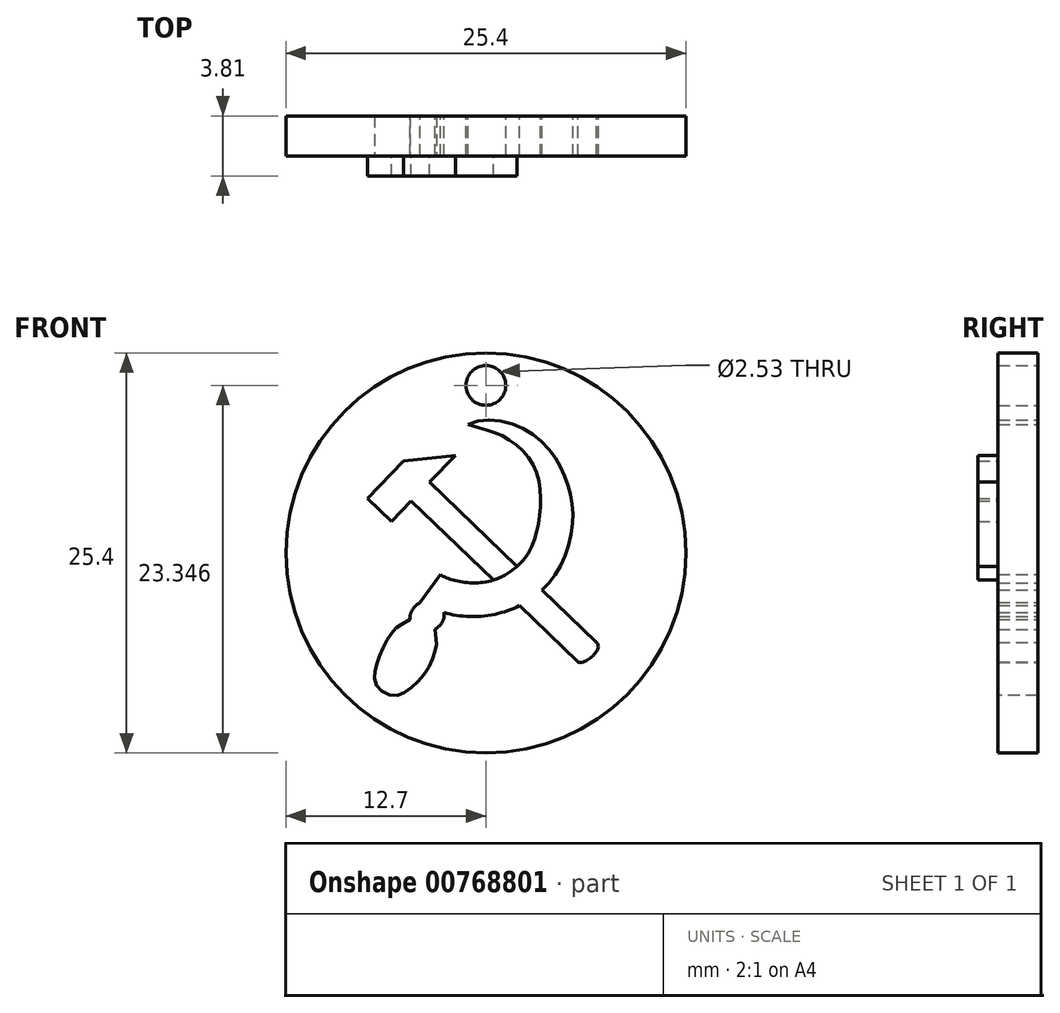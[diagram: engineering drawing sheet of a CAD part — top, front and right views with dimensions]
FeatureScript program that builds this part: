
annotation { "Feature Type Name" : "Feature", "Feature Type Description" : "" }
export const myFeature = defineFeature(function(context is Context, id is Id, definition is map)
    precondition{}
    {
        {
            var Q0;
            Q0=qCreatedBy(makeId("Front.planeOp"),FACE);
            var sketch = newSketch(context, id + "F0", { "sketchPlane" : qUnion([Q0])});
            skCircle(sketch, "E0", {"center": v(0, 0) * mm, "radius": 12.7 * mm});
            skCircle(sketch, "E1", {"center": v(0, 10.65) * mm, "radius": 1.27 * mm});
            skLineSegment(sketch, "E2", {"start": v(-7.53, 3.47) * mm, "end": v(-6, 2) * mm});
            skLineSegment(sketch, "E3", {"start": v(-7.53, 3.47) * mm, "end": v(-5.23, 5.85) * mm});
            skLineSegment(sketch, "E4", {"start": v(-6, 2) * mm, "end": v(-4.74, 3.3) * mm});
            skLineSegment(sketch, "E5", {"start": v(-1.94, 6.2) * mm, "end": v(-5.23, 5.85) * mm});
            skLineSegment(sketch, "E6", {"start": v(-4.74, 3.3) * mm, "end": v(0.47, -1.72) * mm});
            skLineSegment(sketch, "E7", {"start": v(-3.57, 4.51) * mm, "end": v(1.99, -0.84) * mm});
            skFitSpline(sketch, "E8", {"points": [v(7.03, -5.7) * mm, v(5.86, -6.91) * mm], "startDerivative": vector(1.48, -1.28) * mm, "endDerivative": vector(-1, 0.86) * mm});
            skLineSegment(sketch, "E9.trimOffspring", {"start": v(-3.57, 4.51) * mm, "end": v(-1.94, 6.2) * mm});
            skFitSpline(sketch, "E10", {"points": [v(-2.89, -1.37) * mm, v(-0.15, -1.86) * mm, v(2.5, -0.28) * mm, v(3.4, 2.29) * mm, v(3.1, 5.4) * mm, v(0.88, 7.52) * mm, v(-1.13, 8.15) * mm], "startDerivative": vector(9.05, -6.27) * mm, "endDerivative": vector(-9.41, 3.14) * mm});
            skFitSpline(sketch, "E11", {"points": [v(-1.13, 8.15) * mm, v(1.82, 8.15) * mm, v(4.18, 6.36) * mm, v(5.24, 4.2) * mm, v(5.52, 1.99) * mm, v(4.73, -0.8) * mm, v(3.17, -2.69) * mm, v(0.58, -3.9) * mm, v(-2.65, -3.77) * mm], "startDerivative": vector(18.3, 9.86) * mm, "endDerivative": vector(-19.6, 6.72) * mm});
            skLineSegment(sketch, "E12", {"start": v(-2.89, -1.37) * mm, "end": v(-4.2, -3.15) * mm});
            skFitSpline(sketch, "E13", {"points": [v(-2.65, -3.77) * mm, v(-3.23, -4.86) * mm], "startDerivative": vector(0.09, -1.86) * mm, "endDerivative": vector(-0.92, -0.75) * mm});
            skFitSpline(sketch, "E14", {"points": [v(-4.2, -3.15) * mm, v(-4.8, -4.23) * mm], "startDerivative": vector(-1.56, -0.98) * mm, "endDerivative": vector(0.16, -1.07) * mm});
            skFitSpline(sketch, "E15", {"points": [v(-4.8, -4.23) * mm, v(-5.85, -4.92) * mm, v(-6.57, -6.11) * mm, v(-7, -7.4) * mm, v(-6.93, -8.45) * mm, v(-5.8, -9.05) * mm, v(-4.66, -8.48) * mm, v(-3.6, -7.2) * mm, v(-3.16, -5.94) * mm, v(-3.23, -4.86) * mm], "startDerivative": vector(-16.95, -8.14) * mm, "endDerivative": vector(-2.6, 18.44) * mm});
            skLineSegment(sketch, "E16.trimOffspring", {"start": v(2.15, -3.34) * mm, "end": v(5.86, -6.91) * mm});
            skLineSegment(sketch, "E17.trimOffspring", {"start": v(3.56, -2.36) * mm, "end": v(7.03, -5.7) * mm});
            skFitSpline(sketch, "E18.trimOffspring", {"points": [v(-1.13, 8.15) * mm, v(1.82, 8.15) * mm, v(4.18, 6.36) * mm, v(5.24, 4.2) * mm, v(5.52, 1.99) * mm, v(4.73, -0.8) * mm, v(3.17, -2.69) * mm, v(0.58, -3.9) * mm, v(-2.65, -3.77) * mm], "startDerivative": vector(18.3, 9.86) * mm, "endDerivative": vector(-19.6, 6.72) * mm});
            skSolve(sketch);
        }
        {
            var Q0;
            Q0=makeQuery(id+"F0.imprint","IMPRINT",FACE,{"disambiguationData":[TD([[makeQuery(id+"F0.imprint","IMPRINT",EDGE,{"derivedFrom":sQuery(id+"F0.wireOp",EDGE,"E0")}),1.0]])]});
            extrude(context, id + "F1", {"entities" : qUnion([Q0]), "depth" : 2.54 * mm, "offsetDistance" : 25.4 * mm});
        }
        {
            var Q0;
            Q0=makeQuery(id+"F0.imprint","IMPRINT",FACE,{"disambiguationData":[TD([[makeQuery(id+"F0.imprint","IMPRINT",EDGE,{"derivedFrom":sQuery(id+"F0.wireOp",EDGE,"E2")}),1.0]])]});
            extrude(context, id + "F2", {"entities" : qUnion([Q0]), "operationType" : NewBodyOperationType.ADD, "depth" : 3.8 * mm, "offsetDistance" : 25.4 * mm});
        }
    });
